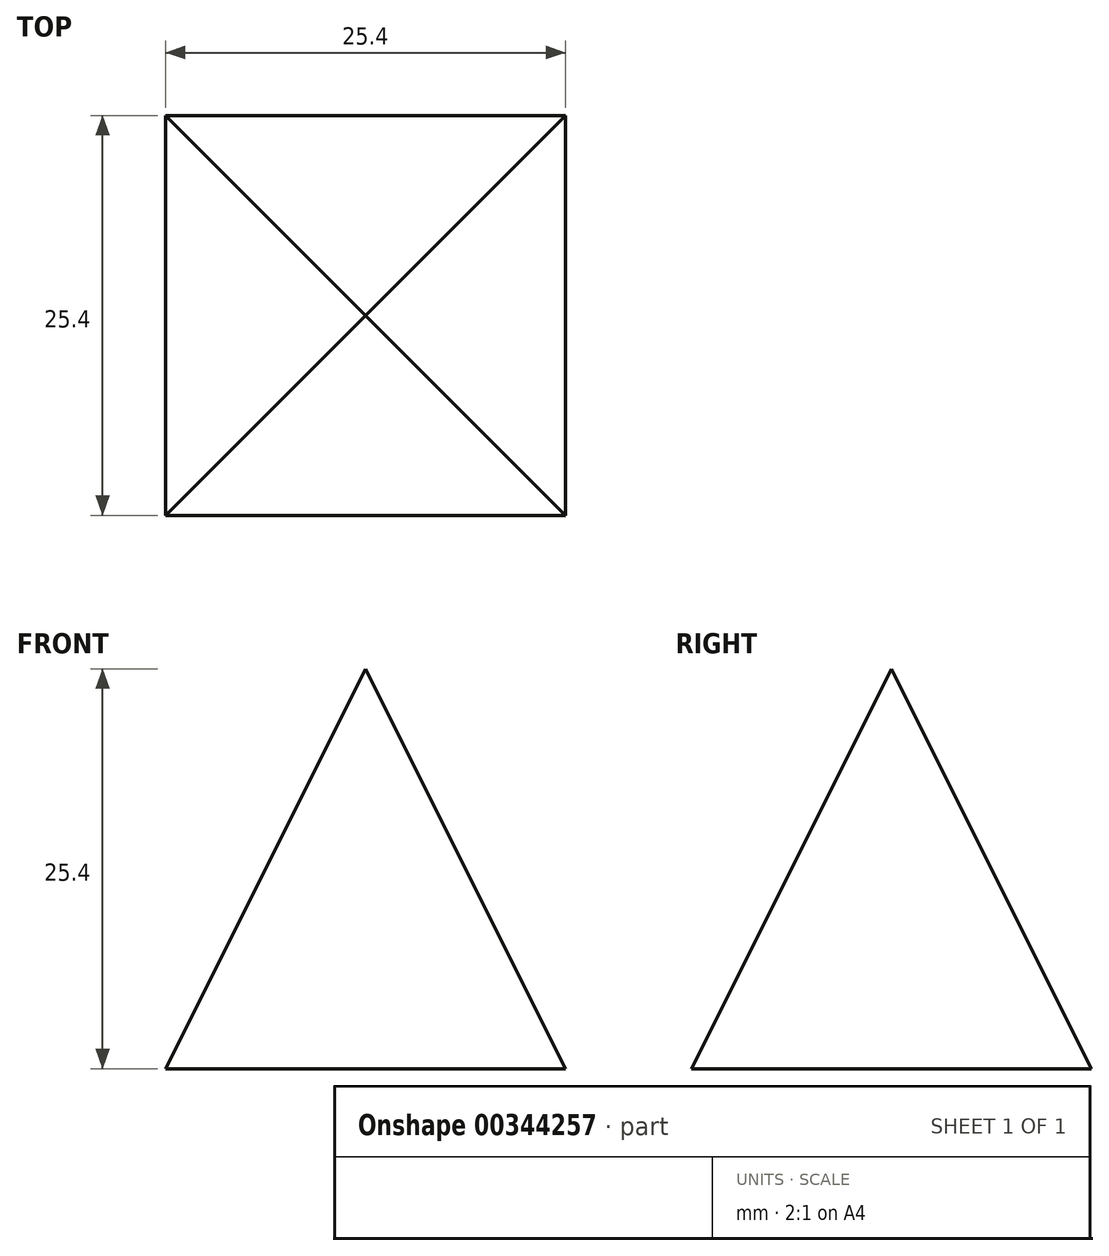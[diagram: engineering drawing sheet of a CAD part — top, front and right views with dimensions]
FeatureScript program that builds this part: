
annotation { "Feature Type Name" : "Feature", "Feature Type Description" : "" }
export const myFeature = defineFeature(function(context is Context, id is Id, definition is map)
    precondition{}
    {
        {
            var Q0;
            Q0=qCreatedBy(makeId("Top.planeOp"),FACE);
            var sketch = newSketch(context, id + "F0", { "sketchPlane" : qUnion([Q0])});
            skLineSegment(sketch, "E0.bottom", {"start": v(-12.7, -12.7) * mm, "end": v(12.7, -12.7) * mm});
            skLineSegment(sketch, "E0.top", {"start": v(-12.7, 12.7) * mm, "end": v(12.7, 12.7) * mm});
            skLineSegment(sketch, "E0.left", {"start": v(-12.7, -12.7) * mm, "end": v(-12.7, 12.7) * mm});
            skLineSegment(sketch, "E0.right", {"start": v(12.7, -12.7) * mm, "end": v(12.7, 12.7) * mm});
            skPoint(sketch, "E0.middle", {"position": v(0, 0) * mm});
            skSolve(sketch);
        }
        {
            var Q0;
            Q0=qCreatedBy(makeId("Front.planeOp"),FACE);
            var sketch = newSketch(context, id + "F1", { "sketchPlane" : qUnion([Q0])});
            skPoint(sketch, "E1", {"position": v(0, 25.4) * mm});
            skSolve(sketch);
        }
        {
            var Q0;
            Q0=makeQuery(id+"F0.imprint","IMPRINT",FACE,{"disambiguationData":[TD([[makeQuery(id+"F0.imprint","IMPRINT",EDGE,{"derivedFrom":sQuery(id+"F0.wireOp",EDGE,"E0.bottom")}),1.0]])]});
            var Q1;
            Q1=sQuery(id+"F1.wireOp",VERTEX,"E1");
            loft(context, id + "F2", {"sheetProfilesArray" : [{ "sheetProfileEntities" : qUnion([Q0]) }, { "sheetProfileEntities" : qUnion([Q1]) }]});
        }
    });
